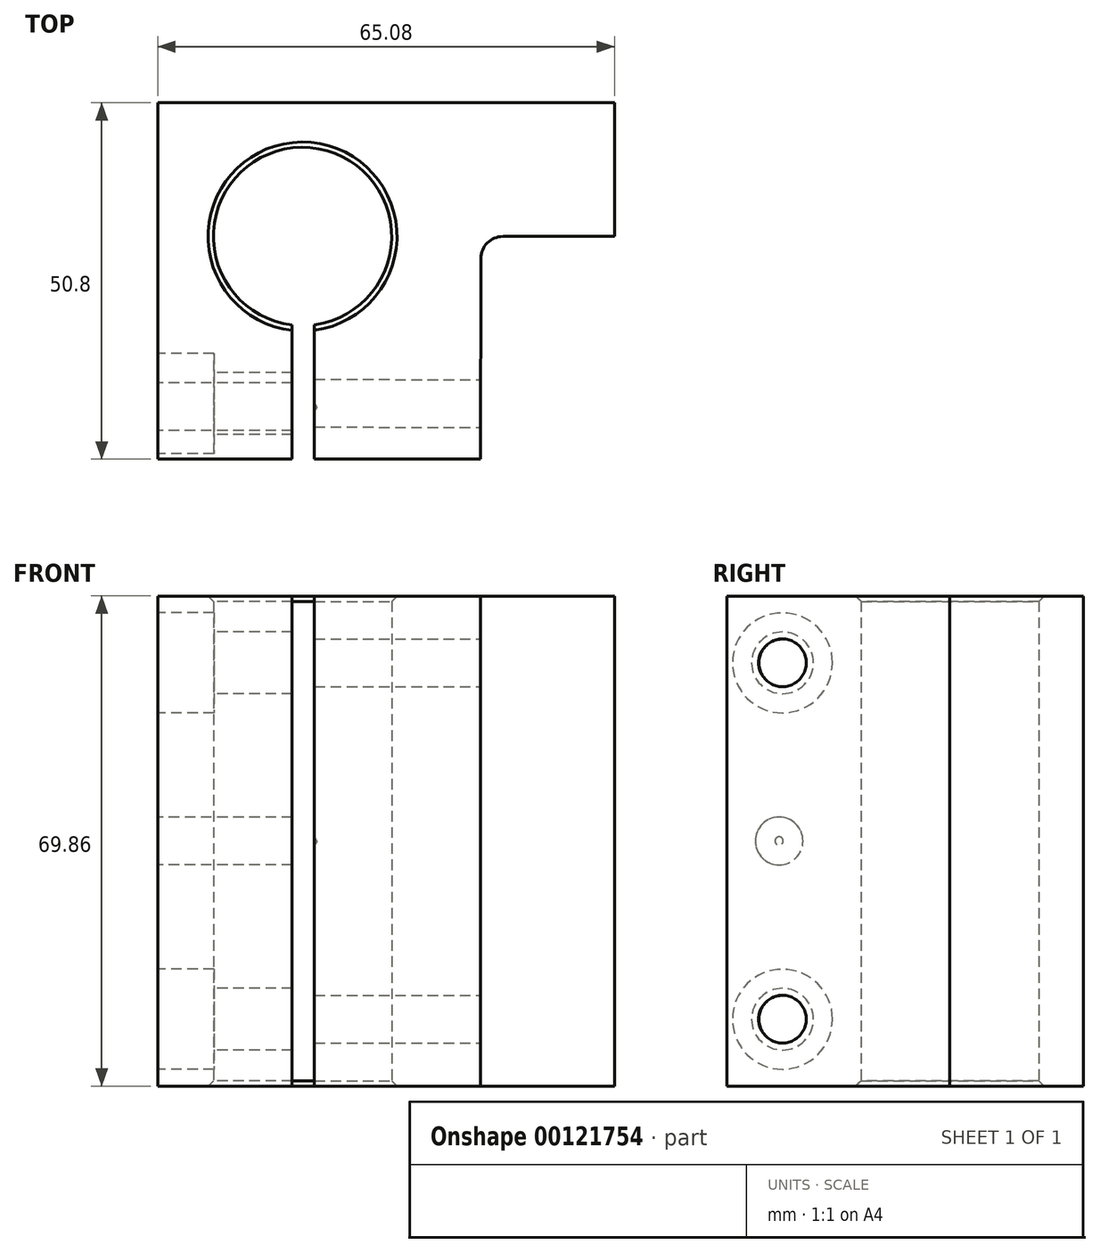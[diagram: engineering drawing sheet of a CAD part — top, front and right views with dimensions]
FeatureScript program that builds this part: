
annotation { "Feature Type Name" : "Feature", "Feature Type Description" : "" }
export const myFeature = defineFeature(function(context is Context, id is Id, definition is map)
    precondition{}
    {
        {
            var Q0;
            Q0=qCreatedBy(makeId("Top.planeOp"),FACE);
            var sketch = newSketch(context, id + "F0", { "sketchPlane" : qUnion([Q0])});
            skLineSegment(sketch, "E0.bottom", {"start": v(-30.13, -31.75) * mm, "end": v(-10.98, -31.75) * mm});
            skLineSegment(sketch, "E0.top", {"start": v(-30.13, 19.05) * mm, "end": v(34.95, 19.05) * mm});
            skLineSegment(sketch, "E0.left", {"start": v(-30.13, -31.75) * mm, "end": v(-30.13, 1.59) * mm});
            skPoint(sketch, "E1.orphan", {"position": v(35.6, -31.75) * mm});
            skArc(sketch, "E2", {"start": v(-22.1, 1.59) * mm, "mid": v(-19.5, -7.83) * mm, "end": v(-10.98, -12.61) * mm});
            skLineSegment(sketch, "E3", {"start": v(34.95, 19.05) * mm, "end": v(34.95, 0) * mm});
            skLineSegment(sketch, "E4", {"start": v(34.95, 0) * mm, "end": v(15.9, 0) * mm});
            skLineSegment(sketch, "E5", {"start": v(15.9, 0) * mm, "end": v(15.85, -31.75) * mm});
            skLineSegment(sketch, "E6.trimOffspring", {"start": v(-30.13, 1.59) * mm, "end": v(-30.13, 19.05) * mm});
            skPoint(sketch, "E7.orphan", {"position": v(-22.1, -1.59) * mm});
            skPoint(sketch, "E8.endSnap0", {"position": v(-7.14, -31.75) * mm});
            skLineSegment(sketch, "E9", {"start": v(-10.98, -31.75) * mm, "end": v(-15.67, -31.75) * mm});
            skLineSegment(sketch, "E10.0", {"start": v(-10.98, -12.61) * mm, "end": v(-10.98, -31.75) * mm});
            skArc(sketch, "E11.trimOffspring", {"start": v(-7.8, -12.59) * mm, "mid": v(-0.56, 9.02) * mm, "end": v(-22.1, 1.59) * mm});
            skLineSegment(sketch, "E12.0", {"start": v(-7.8, -12.59) * mm, "end": v(-7.8, -31.75) * mm});
            skLineSegment(sketch, "E13", {"start": v(-7.8, -31.75) * mm, "end": v(15.85, -31.75) * mm});
            skSolve(sketch);
        }
        {
            var Q0;
            Q0 = qSketchRegion(id + "F0", true);
            extrude(context, id + "F1", {"entities" : qUnion([Q0]), "endBound" : BoundingType.SYMMETRIC, "depth" : 69.85 * mm});
        }
        {
            var Q0;
            Q0=makeQuery(id+"F1.opExtrude","SWEPT_FACE",FACE,{"disambiguationData":[OSD([sQuery(id+"F0.wireOp",EDGE,"E0.left"),sQuery(id+"F0.wireOp",EDGE,"E6.trimOffspring")])]});
            var sketch = newSketch(context, id + "F2", { "sketchPlane" : qUnion([Q0])});
            skCircle(sketch, "E14", {"center": v(23.81, 25.4) * mm, "radius": 3.03 * mm});
            skCircle(sketch, "E15", {"center": v(23.81, 0) * mm, "radius": 4.08 * mm});
            skCircle(sketch, "E16", {"center": v(23.81, -25.4) * mm, "radius": 2.72 * mm});
            skSolve(sketch);
        }
        {
            var Q0;
            Q0=sQuery(id+"F2.wireOp",VERTEX,"E14.center");
            var Q1;
            Q1=sQuery(id+"F2.wireOp",VERTEX,"E16.center");
            var Q2;
            Q2=makeQuery(id+"F1.opExtrude","SWEPT_BODY",BODY,{"disambiguationData":[OSD([sQuery(id+"F0.wireOp",EDGE,"E0.bottom"),sQuery(id+"F0.wireOp",EDGE,"E0.top"),sQuery(id+"F0.wireOp",EDGE,"E0.left"),sQuery(id+"F0.wireOp",EDGE,"E2"),sQuery(id+"F0.wireOp",EDGE,"E3"),sQuery(id+"F0.wireOp",EDGE,"E4"),sQuery(id+"F0.wireOp",EDGE,"E5"),sQuery(id+"F0.wireOp",EDGE,"E6.trimOffspring"),sQuery(id+"F0.wireOp",EDGE,"E9"),sQuery(id+"F0.wireOp",EDGE,"E10.0"),sQuery(id+"F0.wireOp",EDGE,"E11.trimOffspring"),sQuery(id+"F0.wireOp",EDGE,"E12.0"),sQuery(id+"F0.wireOp",EDGE,"E13")])]});
            hole(context, id + "F3", {"style" : HoleStyle.C_BORE, "endStyle" : HoleEndStyle.BLIND, "standardTappedOrClearance" : lookupTablePath({ "standard" : "ISO", "fit" : "Normal", "size" : "M8", "type" : "Clearance" }), "standardBlindInLast" : lookupTablePath({ "fit" : "Standard", "standard" : "ISO", "size" : "M8", "type" : "Clearance" }), "holeDiameter" : 8.8 * mm, "cBoreDiameter" : 14.25 * mm, "cBoreDepth" : 8 * mm, "holeDepth" : 20.64 * mm, "startFromSketch" : true, "locations" : qUnion([Q0, Q1]), "scope" : qUnion([Q2])});
        }
        {
            var Q0;
            Q0=makeQuery(id+"F1.opExtrude","SWEPT_FACE",FACE,{"disambiguationData":[OSD([sQuery(id+"F0.wireOp",EDGE,"E0.left"),sQuery(id+"F0.wireOp",EDGE,"E6.trimOffspring")])]});
            var sketch = newSketch(context, id + "F4", { "sketchPlane" : qUnion([Q0])});
            skCircle(sketch, "E17", {"center": v(24.29, 0) * mm, "radius": 5.89 * mm});
            skSolve(sketch);
        }
        {
            var Q0;
            Q0=sQuery(id+"F4.wireOp",VERTEX,"E17.center");
            var Q1;
            Q1=makeQuery(id+"F1.opExtrude","SWEPT_BODY",BODY,{"disambiguationData":[OSD([sQuery(id+"F0.wireOp",EDGE,"E0.bottom"),sQuery(id+"F0.wireOp",EDGE,"E0.top"),sQuery(id+"F0.wireOp",EDGE,"E0.left"),sQuery(id+"F0.wireOp",EDGE,"E2"),sQuery(id+"F0.wireOp",EDGE,"E3"),sQuery(id+"F0.wireOp",EDGE,"E4"),sQuery(id+"F0.wireOp",EDGE,"E5"),sQuery(id+"F0.wireOp",EDGE,"E6.trimOffspring"),sQuery(id+"F0.wireOp",EDGE,"E9"),sQuery(id+"F0.wireOp",EDGE,"E10.0"),sQuery(id+"F0.wireOp",EDGE,"E11.trimOffspring"),sQuery(id+"F0.wireOp",EDGE,"E12.0"),sQuery(id+"F0.wireOp",EDGE,"E13")])]});
            hole(context, id + "F5", {"style" : HoleStyle.SIMPLE, "endStyle" : HoleEndStyle.BLIND, "standardTappedOrClearance" : lookupTablePath({ "standard" : "ISO", "engagement" : "75%", "pitch" : "1.25 mm", "size" : "M8", "type" : "Tapped" }), "standardBlindInLast" : lookupTablePath({ "standard" : "ISO", "engagement" : "75%", "pitch" : "1.25 mm", "size" : "M8", "type" : "Tapped" }), "holeDiameter" : 6.8 * mm, "holeDepth" : 20.64 * mm, "startFromSketch" : true, "locations" : qUnion([Q0]), "scope" : qUnion([Q1]), "tappedDepth" : 12.7 * mm, "tapClearance" : 3, "majorDiameter" : 8 * mm});
        }
        {
            var Q0;
            Q0=makeQuery(id+"F1.opExtrude","SWEPT_EDGE",EDGE,{"disambiguationData":[OSD([sQuery(id+"F0.wireOp",EDGE,"E4"),sQuery(id+"F0.wireOp",EDGE,"E5")])]});
            fillet(context, id + "F6", {"entities" : qUnion([Q0]), "radius" : 3.17 * mm, "tangentPropagation" : true, "allowEdgeOverflow" : false});
        }
        {
            var Q0;
            Q0=makeQuery(id+"F1.opExtrude","CAP_EDGE",EDGE,{"disambiguationData":[OSD([sQuery(id+"F0.wireOp",EDGE,"E2"),sQuery(id+"F0.wireOp",EDGE,"E11.trimOffspring")])],"isStart":false});
            var Q1;
            Q1=makeQuery(id+"F1.opExtrude","CAP_EDGE",EDGE,{"disambiguationData":[OSD([sQuery(id+"F0.wireOp",EDGE,"E2"),sQuery(id+"F0.wireOp",EDGE,"E11.trimOffspring")])],"isStart":true});
            chamfer(context, id + "F7", {"entities" : qUnion([Q0, Q1]), "width" : 0.76 * mm, "tangentPropagation" : true});
        }
        {
            var Q0;
            Q0=makeQuery(id+"F1.opExtrude","SWEPT_FACE",FACE,{"disambiguationData":[OSD([sQuery(id+"F0.wireOp",EDGE,"E5")])]});
            var sketch = newSketch(context, id + "F8", { "sketchPlane" : qUnion([Q0])});
            skCircle(sketch, "E18", {"center": v(-23.79, 25.4) * mm, "radius": 4.75 * mm});
            skCircle(sketch, "E19", {"center": v(-23.79, -25.4) * mm, "radius": 4.84 * mm});
            skSolve(sketch);
        }
        {
            var Q0;
            Q0=sQuery(id+"F8.wireOp",VERTEX,"E18.center");
            var Q1;
            Q1=sQuery(id+"F8.wireOp",VERTEX,"E19.center");
            var Q2;
            Q2=makeQuery(id+"F1.opExtrude","SWEPT_BODY",BODY,{"disambiguationData":[OSD([sQuery(id+"F0.wireOp",EDGE,"E0.bottom"),sQuery(id+"F0.wireOp",EDGE,"E0.top"),sQuery(id+"F0.wireOp",EDGE,"E0.left"),sQuery(id+"F0.wireOp",EDGE,"E2"),sQuery(id+"F0.wireOp",EDGE,"E3"),sQuery(id+"F0.wireOp",EDGE,"E4"),sQuery(id+"F0.wireOp",EDGE,"E5"),sQuery(id+"F0.wireOp",EDGE,"E6.trimOffspring"),sQuery(id+"F0.wireOp",EDGE,"E9"),sQuery(id+"F0.wireOp",EDGE,"E10.0"),sQuery(id+"F0.wireOp",EDGE,"E11.trimOffspring"),sQuery(id+"F0.wireOp",EDGE,"E12.0"),sQuery(id+"F0.wireOp",EDGE,"E13")])]});
            hole(context, id + "F9", {"style" : HoleStyle.SIMPLE, "endStyle" : HoleEndStyle.THROUGH, "standardTappedOrClearance" : lookupTablePath({ "standard" : "ISO", "engagement" : "75%", "pitch" : "1.25 mm", "size" : "M8", "type" : "Tapped" }), "standardBlindInLast" : lookupTablePath({ "standard" : "ISO", "engagement" : "75%", "pitch" : "1.25 mm", "size" : "M8", "type" : "Tapped" }), "holeDiameter" : 6.8 * mm, "startFromSketch" : true, "locations" : qUnion([Q0, Q1]), "scope" : qUnion([Q2]), "isTappedThrough" : true, "majorDiameter" : 8 * mm, "showTappedDepth" : true});
        }
    });
